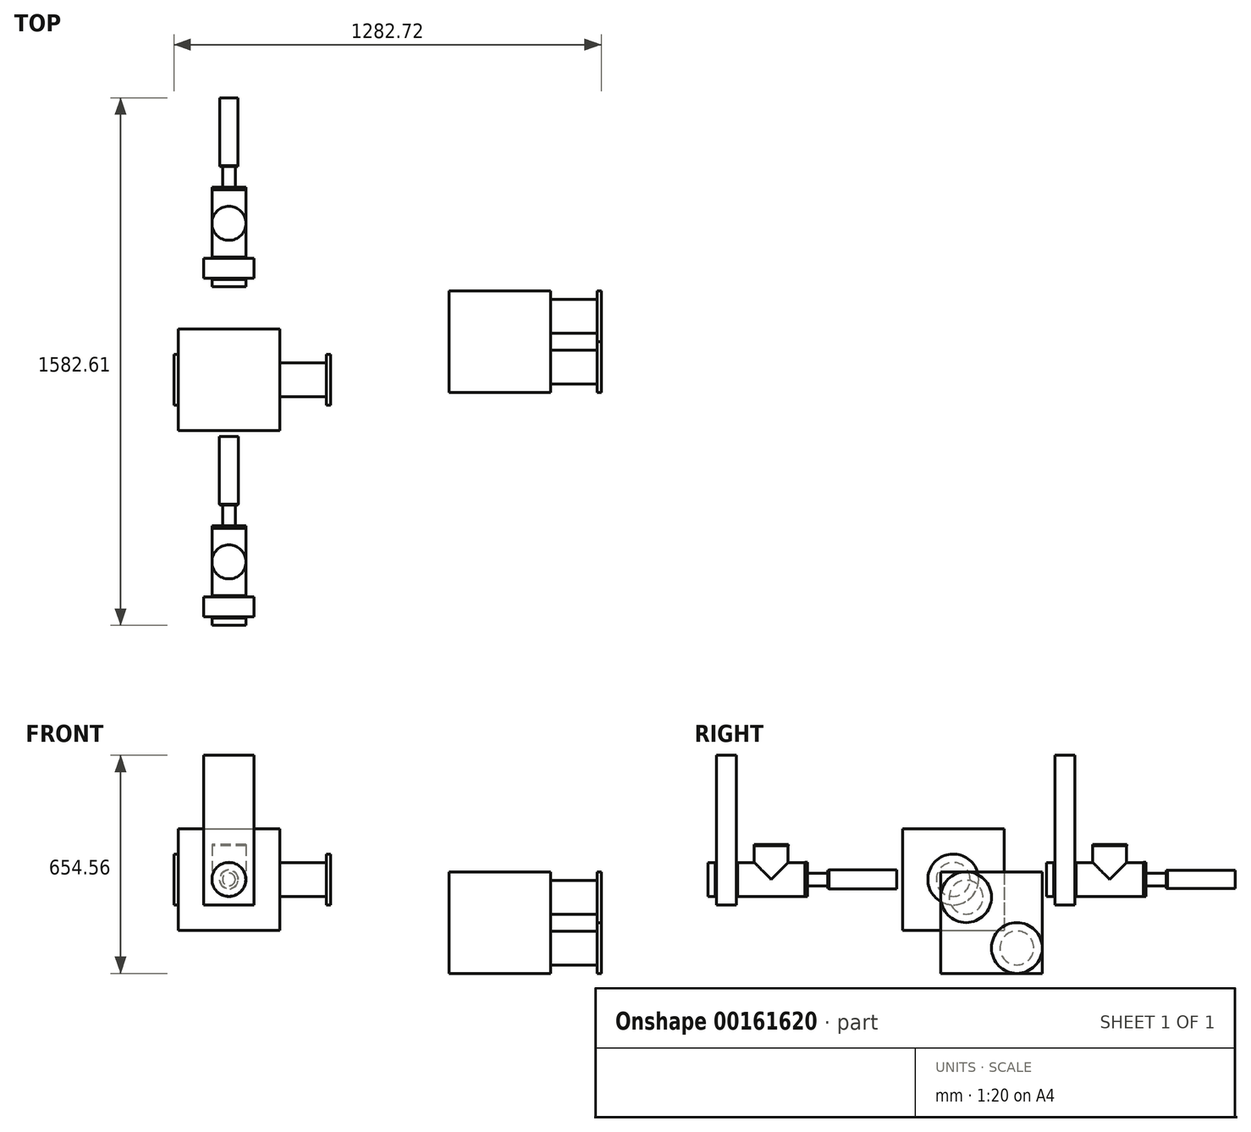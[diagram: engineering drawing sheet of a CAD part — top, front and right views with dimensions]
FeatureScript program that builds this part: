
annotation { "Feature Type Name" : "Feature", "Feature Type Description" : "" }
export const myFeature = defineFeature(function(context is Context, id is Id, definition is map)
    precondition{}
    {
        {
            var Q0;
            Q0=qCreatedBy(makeId("Top.planeOp"),FACE);
            var sketch = newSketch(context, id + "F0", { "sketchPlane" : qUnion([Q0])});
            skLineSegment(sketch, "E0.bottom", {"start": v(-143.78, -114.64) * mm, "end": v(161.02, -114.64) * mm});
            skLineSegment(sketch, "E0.top", {"start": v(-143.78, 190.16) * mm, "end": v(161.02, 190.16) * mm});
            skLineSegment(sketch, "E0.left", {"start": v(-143.78, -114.64) * mm, "end": v(-143.78, 190.16) * mm});
            skLineSegment(sketch, "E0.right", {"start": v(161.02, -114.64) * mm, "end": v(161.02, 190.16) * mm});
            skSolve(sketch);
        }
        {
            var Q0;
            Q0 = qSketchRegion(id + "F0", true);
            var Q1;
            Q1=makeQuery(id+"F0.imprint","IMPRINT",FACE,{"disambiguationData":[TD([[makeQuery(id+"F0.imprint","IMPRINT",EDGE,{"derivedFrom":sQuery(id+"F0.wireOp",EDGE,"E0.bottom")}),1.0]])]});
            extrude(context, id + "F1", {"entities" : qUnion([Q0, Q1]), "depth" : 304.8 * mm});
        }
        {
            var Q0;
            Q0=makeQuery(id+"F1.opExtrude","SWEPT_FACE",FACE,{"disambiguationData":[OSD([sQuery(id+"F0.wireOp",EDGE,"E0.right")])]});
            cPlane(context, id + "F2", {"entities" : qUnion([Q0]), "cplaneType" : CPlaneType.OFFSET, "offset" : 0 * mm, "width" : 152.4 * mm, "height" : 152.4 * mm});
        }
        {
            var Q0;
            Q0=qCreatedBy(id+"F2.planeOp",FACE);
            var sketch = newSketch(context, id + "F3", { "sketchPlane" : qUnion([Q0])});
            skCircle(sketch, "E1", {"center": v(37.76, 152.4) * mm, "radius": 50.8 * mm});
            skSolve(sketch);
        }
        {
            var Q0;
            Q0=makeQuery(id+"F3.imprint","IMPRINT",FACE,{"disambiguationData":[TD([[makeQuery(id+"F3.imprint","IMPRINT",EDGE,{"derivedFrom":sQuery(id+"F3.wireOp",EDGE,"E1")}),1.0]])]});
            extrude(context, id + "F4", {"entities" : qUnion([Q0]), "operationType" : NewBodyOperationType.ADD, "depth" : 139.7 * mm});
        }
        {
            var Q0;
            Q0=makeQuery(id+"F4.opExtrude","CAP_FACE",FACE,{"disambiguationData":[OSD([sQuery(id+"F3.wireOp",EDGE,"E1")])],"isStart":false});
            cPlane(context, id + "F5", {"entities" : qUnion([Q0]), "cplaneType" : CPlaneType.OFFSET, "offset" : 0 * mm, "width" : 152.4 * mm, "height" : 152.4 * mm});
        }
        {
            var Q0;
            Q0=qCreatedBy(id+"F5.planeOp",FACE);
            var sketch = newSketch(context, id + "F6", { "sketchPlane" : qUnion([Q0])});
            skCircle(sketch, "E2", {"center": v(37.76, 152.4) * mm, "radius": 76.2 * mm});
            skSolve(sketch);
        }
        {
            var Q0;
            Q0 = qSketchRegion(id + "F6", true);
            extrude(context, id + "F7", {"entities" : qUnion([Q0]), "operationType" : NewBodyOperationType.ADD, "depth" : 12.7 * mm});
        }
        {
            var Q0;
            Q0=makeQuery(id+"F1.opExtrude","SWEPT_FACE",FACE,{"disambiguationData":[OSD([sQuery(id+"F0.wireOp",EDGE,"E0.left")])]});
            cPlane(context, id + "F8", {"entities" : qUnion([Q0]), "cplaneType" : CPlaneType.OFFSET, "offset" : 0 * mm, "width" : 152.4 * mm, "height" : 152.4 * mm});
        }
        {
            var Q0;
            Q0=qCreatedBy(id+"F8.planeOp",FACE);
            var sketch = newSketch(context, id + "F9", { "sketchPlane" : qUnion([Q0])});
            skCircle(sketch, "E3", {"center": v(-37.76, 152.4) * mm, "radius": 50.8 * mm});
            skSolve(sketch);
        }
        {
            var Q0;
            Q0 = qSketchRegion(id + "F9", true);
            extrude(context, id + "F10", {"entities" : qUnion([Q0]), "operationType" : NewBodyOperationType.ADD, "depth" : 0.03 * mm});
        }
        {
            var Q0;
            Q0=makeQuery(id+"F10.opExtrude","CAP_FACE",FACE,{"disambiguationData":[OSD([sQuery(id+"F9.wireOp",EDGE,"E3")])],"isStart":false});
            cPlane(context, id + "F11", {"entities" : qUnion([Q0]), "cplaneType" : CPlaneType.OFFSET, "offset" : 0 * mm, "width" : 152.4 * mm, "height" : 152.4 * mm});
        }
        {
            var Q0;
            Q0=qCreatedBy(id+"F11.planeOp",FACE);
            var sketch = newSketch(context, id + "F12", { "sketchPlane" : qUnion([Q0])});
            skCircle(sketch, "E4", {"center": v(-37.76, 152.4) * mm, "radius": 76.2 * mm});
            skSolve(sketch);
        }
        {
            var Q0;
            Q0 = qSketchRegion(id + "F12", true);
            extrude(context, id + "F13", {"entities" : qUnion([Q0]), "operationType" : NewBodyOperationType.ADD, "depth" : 12.7 * mm});
        }
        {
            var Q0;
            Q0=makeQuery(id+"F1.opExtrude","SWEPT_FACE",FACE,{"disambiguationData":[OSD([sQuery(id+"F0.wireOp",EDGE,"E0.top")])]});
            cPlane(context, id + "F14", {"entities" : qUnion([Q0]), "cplaneType" : CPlaneType.OFFSET, "offset" : 127 * mm, "width" : 152.4 * mm, "height" : 152.4 * mm});
        }
        {
            var Q0;
            Q0=qCreatedBy(id+"F14.planeOp",FACE);
            var sketch = newSketch(context, id + "F15", { "sketchPlane" : qUnion([Q0])});
            skCircle(sketch, "E5", {"center": v(-8.62, 152.4) * mm, "radius": 50.8 * mm});
            skSolve(sketch);
        }
        {
            var Q0;
            Q0 = qSketchRegion(id + "F15", true);
            extrude(context, id + "F16", {"entities" : qUnion([Q0]), "depth" : 21.59 * mm});
        }
        {
            var Q0;
            Q0=makeQuery(id+"F16.opExtrude","CAP_FACE",FACE,{"disambiguationData":[OSD([sQuery(id+"F15.wireOp",EDGE,"E5")])],"isStart":false});
            cPlane(context, id + "F17", {"entities" : qUnion([Q0]), "cplaneType" : CPlaneType.OFFSET, "offset" : 0 * mm, "width" : 152.4 * mm, "height" : 152.4 * mm});
        }
        {
            var Q0;
            Q0=qCreatedBy(id+"F17.planeOp",FACE);
            var sketch = newSketch(context, id + "F18", { "sketchPlane" : qUnion([Q0])});
            skCircle(sketch, "E6", {"center": v(-8.62, 152.4) * mm, "radius": 51 * mm});
            skSolve(sketch);
        }
        {
            var Q0;
            Q0 = qSketchRegion(id + "F18", true);
            extrude(context, id + "F19", {"entities" : qUnion([Q0]), "operationType" : NewBodyOperationType.ADD, "depth" : 3.8 * mm});
        }
        {
            var Q0;
            Q0=makeQuery(id+"F19.opExtrude","CAP_FACE",FACE,{"disambiguationData":[OSD([sQuery(id+"F18.wireOp",EDGE,"E6")])],"isStart":false});
            cPlane(context, id + "F20", {"entities" : qUnion([Q0]), "cplaneType" : CPlaneType.OFFSET, "offset" : 0 * mm, "width" : 152.4 * mm, "height" : 152.4 * mm});
        }
        {
            var Q0;
            Q0=qCreatedBy(id+"F20.planeOp",FACE);
            var sketch = newSketch(context, id + "F21", { "sketchPlane" : qUnion([Q0])});
            skLineSegment(sketch, "E7.bottom", {"start": v(-84.57, 525.02) * mm, "end": v(67.32, 525.02) * mm});
            skLineSegment(sketch, "E7.top", {"start": v(-84.57, 76.2) * mm, "end": v(67.32, 76.2) * mm});
            skLineSegment(sketch, "E7.left", {"start": v(-84.57, 525.02) * mm, "end": v(-84.57, 76.2) * mm});
            skLineSegment(sketch, "E7.right", {"start": v(67.32, 525.02) * mm, "end": v(67.32, 76.2) * mm});
            skSolve(sketch);
        }
        {
            var Q0;
            Q0 = qSketchRegion(id + "F21", true);
            extrude(context, id + "F22", {"entities" : qUnion([Q0]), "operationType" : NewBodyOperationType.ADD, "depth" : 59.94 * mm});
        }
        {
            var Q0;
            Q0=makeQuery(id+"F22.opExtrude","CAP_FACE",FACE,{"disambiguationData":[OSD([sQuery(id+"F21.wireOp",EDGE,"E7.bottom"),sQuery(id+"F21.wireOp",EDGE,"E7.top"),sQuery(id+"F21.wireOp",EDGE,"E7.left"),sQuery(id+"F21.wireOp",EDGE,"E7.right")])],"isStart":false});
            cPlane(context, id + "F23", {"entities" : qUnion([Q0]), "cplaneType" : CPlaneType.OFFSET, "offset" : 0 * mm, "width" : 152.4 * mm, "height" : 152.4 * mm});
        }
        {
            var Q0;
            Q0=qCreatedBy(id+"F23.planeOp",FACE);
            var sketch = newSketch(context, id + "F24", { "sketchPlane" : qUnion([Q0])});
            skCircle(sketch, "E8", {"center": v(-8.62, 152.4) * mm, "radius": 51 * mm});
            skSolve(sketch);
        }
        {
            var Q0;
            Q0 = qSketchRegion(id + "F24", true);
            extrude(context, id + "F25", {"entities" : qUnion([Q0]), "operationType" : NewBodyOperationType.ADD, "depth" : 3.8 * mm});
        }
        {
            var Q0;
            Q0=makeQuery(id+"F25.opExtrude","CAP_FACE",FACE,{"disambiguationData":[OSD([sQuery(id+"F24.wireOp",EDGE,"E8")])],"isStart":false});
            cPlane(context, id + "F26", {"entities" : qUnion([Q0]), "cplaneType" : CPlaneType.OFFSET, "offset" : 0 * mm, "width" : 152.4 * mm, "height" : 152.4 * mm});
        }
        {
            var Q0;
            Q0=qCreatedBy(id+"F26.planeOp",FACE);
            var sketch = newSketch(context, id + "F27", { "sketchPlane" : qUnion([Q0])});
            skCircle(sketch, "E9", {"center": v(-8.62, 152.4) * mm, "radius": 50.8 * mm});
            skSolve(sketch);
        }
        {
            var Q0;
            Q0 = qSketchRegion(id + "F27", true);
            extrude(context, id + "F28", {"entities" : qUnion([Q0]), "operationType" : NewBodyOperationType.ADD, "depth" : 202.18 * mm});
        }
        {
            var Q0;
            Q0=makeQuery(id+"F28.opExtrude","CAP_FACE",FACE,{"disambiguationData":[OSD([sQuery(id+"F27.wireOp",EDGE,"E9")])],"isStart":false});
            cPlane(context, id + "F29", {"entities" : qUnion([Q0]), "cplaneType" : CPlaneType.OFFSET, "offset" : 0 * mm, "width" : 152.4 * mm, "height" : 152.4 * mm});
        }
        {
            var Q0;
            Q0=qCreatedBy(id+"F29.planeOp",FACE);
            var sketch = newSketch(context, id + "F30", { "sketchPlane" : qUnion([Q0])});
            skCircle(sketch, "E10", {"center": v(-8.62, 152.4) * mm, "radius": 51 * mm});
            skSolve(sketch);
        }
        {
            var Q0;
            Q0 = qSketchRegion(id + "F30", true);
            extrude(context, id + "F31", {"entities" : qUnion([Q0]), "operationType" : NewBodyOperationType.ADD, "depth" : 3.8 * mm});
        }
        {
            var Q0;
            Q0=makeQuery(id+"F22.opExtrude","SWEPT_FACE",FACE,{"disambiguationData":[OSD([sQuery(id+"F21.wireOp",EDGE,"E7.bottom")])]});
            cPlane(context, id + "F32", {"entities" : qUnion([Q0]), "cplaneType" : CPlaneType.OFFSET, "offset" : 372.62 * mm, "oppositeDirection" : true, "width" : 152.4 * mm, "height" : 152.4 * mm});
        }
        {
            var Q0;
            Q0=qCreatedBy(id+"F32.planeOp",FACE);
            var sketch = newSketch(context, id + "F33", { "sketchPlane" : qUnion([Q0])});
            skCircle(sketch, "E11", {"center": v(8.62, 507.4) * mm, "radius": 50.8 * mm});
            skSolve(sketch);
        }
        {
            var Q0;
            Q0 = qSketchRegion(id + "F33", true);
            extrude(context, id + "F34", {"entities" : qUnion([Q0]), "operationType" : NewBodyOperationType.ADD, "depth" : 101.1 * mm});
        }
        {
            var Q0;
            Q0=makeQuery(id+"F34.opExtrude","CAP_FACE",FACE,{"disambiguationData":[OSD([sQuery(id+"F33.wireOp",EDGE,"E11")])],"isStart":false});
            cPlane(context, id + "F35", {"entities" : qUnion([Q0]), "cplaneType" : CPlaneType.OFFSET, "offset" : 0 * mm, "width" : 152.4 * mm, "height" : 152.4 * mm});
        }
        {
            var Q0;
            Q0=qCreatedBy(id+"F35.planeOp",FACE);
            var sketch = newSketch(context, id + "F36", { "sketchPlane" : qUnion([Q0])});
            skCircle(sketch, "E12", {"center": v(8.62, 507.4) * mm, "radius": 51 * mm});
            skSolve(sketch);
        }
        {
            var Q0;
            Q0 = qSketchRegion(id + "F36", true);
            extrude(context, id + "F37", {"entities" : qUnion([Q0]), "operationType" : NewBodyOperationType.ADD, "depth" : 3.8 * mm});
        }
        {
            var Q0;
            Q0=makeQuery(id+"F31.opExtrude","CAP_FACE",FACE,{"disambiguationData":[OSD([sQuery(id+"F30.wireOp",EDGE,"E10")])],"isStart":false});
            cPlane(context, id + "F38", {"entities" : qUnion([Q0]), "cplaneType" : CPlaneType.OFFSET, "offset" : 0 * mm, "width" : 152.4 * mm, "height" : 152.4 * mm});
        }
        {
            var Q0;
            Q0=qCreatedBy(id+"F38.planeOp",FACE);
            var sketch = newSketch(context, id + "F39", { "sketchPlane" : qUnion([Q0])});
            skCircle(sketch, "E13", {"center": v(-8.62, 152.4) * mm, "radius": 51 * mm});
            skSolve(sketch);
        }
        {
            var Q0;
            Q0 = qSketchRegion(id + "F39", true);
            extrude(context, id + "F40", {"entities" : qUnion([Q0]), "operationType" : NewBodyOperationType.ADD, "depth" : 3.8 * mm});
        }
        {
            var Q0;
            Q0=makeQuery(id+"F40.opExtrude","CAP_FACE",FACE,{"disambiguationData":[OSD([sQuery(id+"F39.wireOp",EDGE,"E13")])],"isStart":false});
            cPlane(context, id + "F41", {"entities" : qUnion([Q0]), "cplaneType" : CPlaneType.OFFSET, "offset" : 0 * mm, "width" : 152.4 * mm, "height" : 152.4 * mm});
        }
        {
            var Q0;
            Q0=qCreatedBy(id+"F41.planeOp",FACE);
            var sketch = newSketch(context, id + "F42", { "sketchPlane" : qUnion([Q0])});
            skCircle(sketch, "E14", {"center": v(-8.62, 152.4) * mm, "radius": 19.05 * mm});
            skSolve(sketch);
        }
        {
            var Q0;
            Q0 = qSketchRegion(id + "F42", true);
            extrude(context, id + "F43", {"entities" : qUnion([Q0]), "operationType" : NewBodyOperationType.ADD, "depth" : 61.4 * mm});
        }
        {
            var Q0;
            Q0=makeQuery(id+"F43.opExtrude","CAP_FACE",FACE,{"disambiguationData":[OSD([sQuery(id+"F42.wireOp",EDGE,"E14")])],"isStart":false});
            cPlane(context, id + "F44", {"entities" : qUnion([Q0]), "cplaneType" : CPlaneType.OFFSET, "offset" : 0 * mm, "width" : 152.4 * mm, "height" : 152.4 * mm});
        }
        {
            var Q0;
            Q0=qCreatedBy(id+"F44.planeOp",FACE);
            var sketch = newSketch(context, id + "F45", { "sketchPlane" : qUnion([Q0])});
            skCircle(sketch, "E15", {"center": v(-8.62, 152.4) * mm, "radius": 27.43 * mm});
            skSolve(sketch);
        }
        {
            var Q0;
            Q0 = qSketchRegion(id + "F45", true);
            extrude(context, id + "F46", {"entities" : qUnion([Q0]), "operationType" : NewBodyOperationType.ADD, "depth" : 3.05 * mm});
        }
        {
            var Q0;
            Q0=makeQuery(id+"F16.opExtrude","SWEPT_BODY",BODY,{"disambiguationData":[OSD([sQuery(id+"F15.wireOp",EDGE,"E5")])]});
            transform(context, id + "F47", {"entities" : qUnion([Q0]), "transformType" : TransformType.TRANSLATION_3D, "dx" : 0 * mm, "dy" : -1016 * mm, "dz" : 0 * mm, "makeCopy" : true});
        }
        {
            var Q0;
            Q0=qCreatedBy(id+"F2.planeOp",FACE);
            cPlane(context, id + "F48", {"entities" : qUnion([Q0]), "cplaneType" : CPlaneType.OFFSET, "offset" : 508 * mm, "width" : 152.4 * mm, "height" : 152.4 * mm});
        }
        {
            var Q0;
            Q0=qCreatedBy(id+"F48.planeOp",FACE);
            var sketch = newSketch(context, id + "F49", { "sketchPlane" : qUnion([Q0])});
            skLineSegment(sketch, "E16.bottom", {"start": v(0, 175.26) * mm, "end": v(304.8, 175.26) * mm});
            skLineSegment(sketch, "E16.top", {"start": v(0, -129.54) * mm, "end": v(304.8, -129.54) * mm});
            skLineSegment(sketch, "E16.left", {"start": v(0, 175.26) * mm, "end": v(0, -129.54) * mm});
            skLineSegment(sketch, "E16.right", {"start": v(304.8, 175.26) * mm, "end": v(304.8, -129.54) * mm});
            skSolve(sketch);
        }
        {
            var Q0;
            Q0 = qSketchRegion(id + "F49", true);
            extrude(context, id + "F50", {"entities" : qUnion([Q0]), "depth" : 304.8 * mm});
        }
        {
            var Q0;
            Q0=makeQuery(id+"F50.opExtrude","CAP_FACE",FACE,{"disambiguationData":[OSD([sQuery(id+"F49.wireOp",EDGE,"E16.bottom"),sQuery(id+"F49.wireOp",EDGE,"E16.top"),sQuery(id+"F49.wireOp",EDGE,"E16.left"),sQuery(id+"F49.wireOp",EDGE,"E16.right")])],"isStart":false});
            cPlane(context, id + "F51", {"entities" : qUnion([Q0]), "cplaneType" : CPlaneType.OFFSET, "offset" : 0 * mm, "width" : 152.4 * mm, "height" : 152.4 * mm});
        }
        {
            var Q0;
            Q0=qCreatedBy(id+"F51.planeOp",FACE);
            var sketch = newSketch(context, id + "F52", { "sketchPlane" : qUnion([Q0])});
            skCircle(sketch, "E17", {"center": v(76.2, 99.06) * mm, "radius": 50.8 * mm});
            skCircle(sketch, "E18", {"center": v(228.6, -53.34) * mm, "radius": 50.8 * mm});
            skSolve(sketch);
        }
        {
            var Q0;
            Q0 = qSketchRegion(id + "F52", true);
            extrude(context, id + "F53", {"entities" : qUnion([Q0]), "operationType" : NewBodyOperationType.ADD, "depth" : 139.7 * mm});
        }
        {
            var Q0;
            Q0=makeQuery(id+"F53.opExtrude","CAP_FACE",FACE,{"disambiguationData":[OSD([sQuery(id+"F52.wireOp",EDGE,"E17")])],"isStart":false});
            cPlane(context, id + "F54", {"entities" : qUnion([Q0]), "cplaneType" : CPlaneType.OFFSET, "offset" : 0 * mm, "width" : 152.4 * mm, "height" : 152.4 * mm});
        }
        {
            var Q0;
            Q0=qCreatedBy(id+"F54.planeOp",FACE);
            var sketch = newSketch(context, id + "F55", { "sketchPlane" : qUnion([Q0])});
            skCircle(sketch, "E19", {"center": v(76.2, 99.06) * mm, "radius": 76.2 * mm});
            skCircle(sketch, "E20", {"center": v(228.6, -53.34) * mm, "radius": 76.2 * mm});
            skSolve(sketch);
        }
        {
            var Q0;
            Q0 = qSketchRegion(id + "F55", true);
            extrude(context, id + "F56", {"entities" : qUnion([Q0]), "operationType" : NewBodyOperationType.ADD, "depth" : 12.7 * mm});
        }
        {
            var Q0;
            Q0=makeQuery(id+"F46.opExtrude","CAP_FACE",FACE,{"disambiguationData":[OSD([sQuery(id+"F45.wireOp",EDGE,"E15")])],"isStart":false});
            var sketch = newSketch(context, id + "F57", { "sketchPlane" : qUnion([Q0])});
            skCircle(sketch, "E21", {"center": v(-8.62, 152.4) * mm, "radius": 27.38 * mm});
            skSolve(sketch);
        }
        {
            var Q0;
            Q0 = qSketchRegion(id + "F57", true);
            extrude(context, id + "F58", {"entities" : qUnion([Q0]), "operationType" : NewBodyOperationType.ADD, "depth" : 203.2 * mm});
        }
        {
            var Q0;
            Q0=makeQuery(id+"F47.opPattern","COPY",FACE,{"derivedFrom":makeQuery(id+"F46.opExtrude","CAP_FACE",FACE,{"disambiguationData":[OSD([sQuery(id+"F45.wireOp",EDGE,"E15")])],"isStart":false}),"instanceName":"1"});
            var sketch = newSketch(context, id + "F59", { "sketchPlane" : qUnion([Q0])});
            skCircle(sketch, "E22", {"center": v(-8.62, 152.4) * mm, "radius": 28.57 * mm});
            skSolve(sketch);
        }
        {
            var Q0;
            Q0 = qSketchRegion(id + "F59", true);
            extrude(context, id + "F60", {"entities" : qUnion([Q0]), "operationType" : NewBodyOperationType.ADD, "depth" : 203.2 * mm});
        }
        {
            var Q0;
            Q0 = qSketchRegion(id + "F59", true);
            extrude(context, id + "F61", {"entities" : qUnion([Q0]), "operationType" : NewBodyOperationType.ADD, "depth" : 203.2 * mm});
        }
    });
